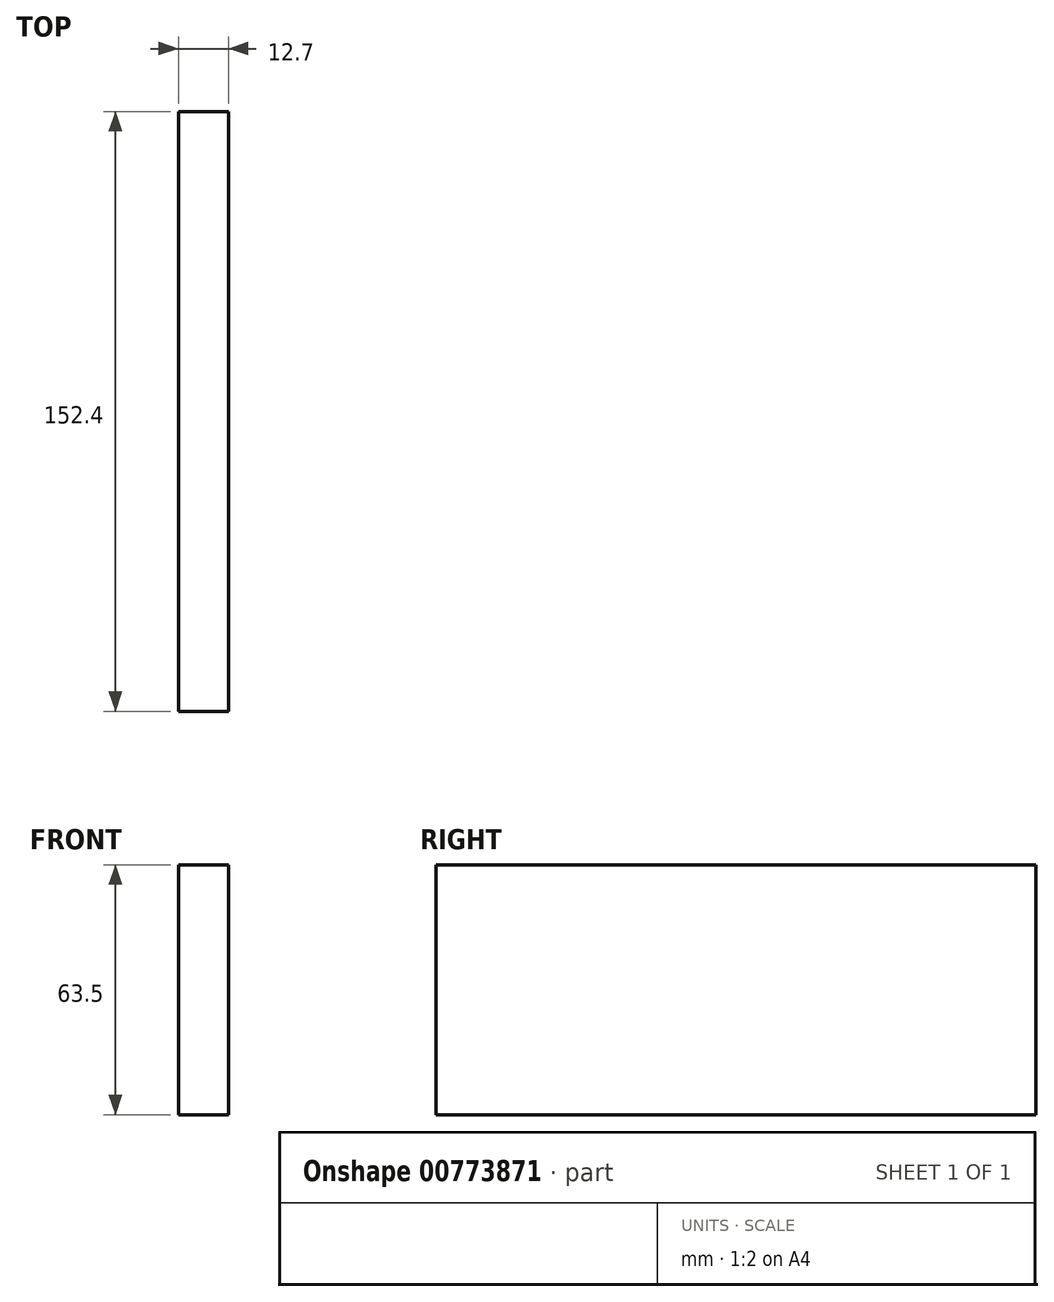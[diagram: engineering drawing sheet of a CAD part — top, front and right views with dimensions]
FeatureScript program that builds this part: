
annotation { "Feature Type Name" : "Feature", "Feature Type Description" : "" }
export const myFeature = defineFeature(function(context is Context, id is Id, definition is map)
    precondition{}
    {
        {
            var Q0;
            Q0=qCreatedBy(makeId("Right.planeOp"),FACE);
            var sketch = newSketch(context, id + "F0", { "sketchPlane" : qUnion([Q0])});
            skLineSegment(sketch, "E0.bottom", {"start": v(0, 0) * mm, "end": v(-152.4, 0) * mm});
            skLineSegment(sketch, "E0.top", {"start": v(0, 63.5) * mm, "end": v(-152.4, 63.5) * mm});
            skLineSegment(sketch, "E0.left", {"start": v(0, 0) * mm, "end": v(0, 63.5) * mm});
            skLineSegment(sketch, "E0.right", {"start": v(-152.4, 0) * mm, "end": v(-152.4, 63.5) * mm});
            skSolve(sketch);
        }
        {
            var Q0;
            Q0 = qSketchRegion(id + "F0", true);
            extrude(context, id + "F1", {"entities" : qUnion([Q0]), "depth" : 12.7 * mm, "offsetDistance" : 25.4 * mm});
        }
    });
